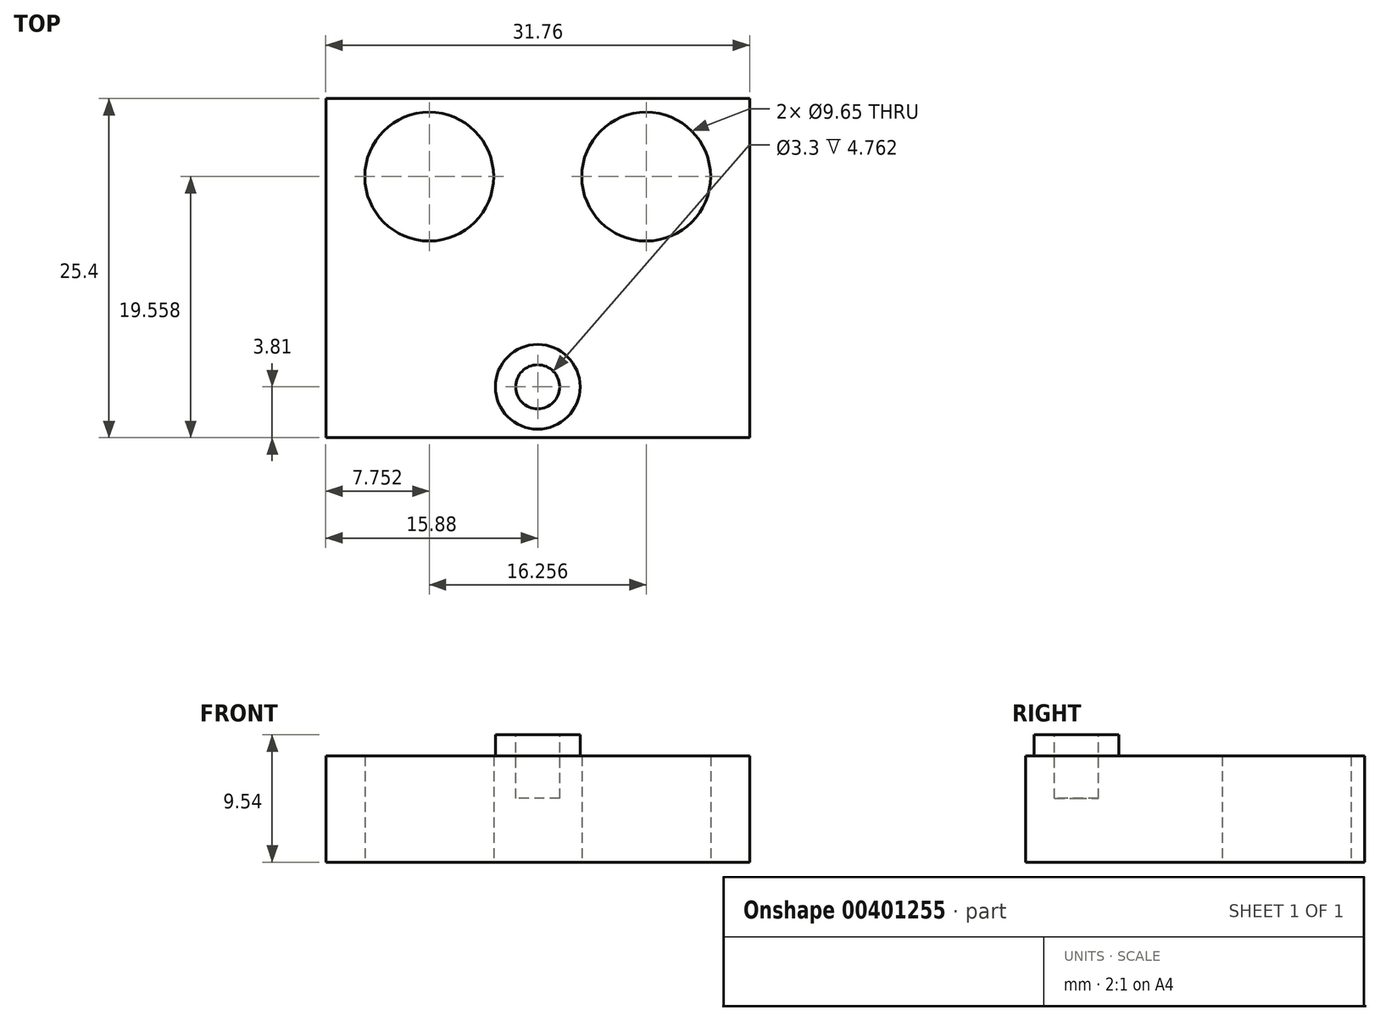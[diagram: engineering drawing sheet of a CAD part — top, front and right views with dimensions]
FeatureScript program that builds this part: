
annotation { "Feature Type Name" : "Feature", "Feature Type Description" : "" }
export const myFeature = defineFeature(function(context is Context, id is Id, definition is map)
    precondition{}
    {
        {
            var Q0;
            Q0=qCreatedBy(makeId("Top.planeOp"),FACE);
            var sketch = newSketch(context, id + "F0", { "sketchPlane" : qUnion([Q0])});
            skLineSegment(sketch, "E0.bottom", {"start": v(-15.88, 12.7) * mm, "end": v(15.88, 12.7) * mm});
            skLineSegment(sketch, "E0.top", {"start": v(-15.88, -12.7) * mm, "end": v(15.88, -12.7) * mm});
            skLineSegment(sketch, "E0.left", {"start": v(-15.88, 12.7) * mm, "end": v(-15.88, -12.7) * mm});
            skLineSegment(sketch, "E0.right", {"start": v(15.88, 12.7) * mm, "end": v(15.88, -12.7) * mm});
            skPoint(sketch, "E0.middle", {"position": v(0, 0) * mm});
            skCircle(sketch, "E1", {"center": v(-8.13, 6.86) * mm, "radius": 4.83 * mm});
            skCircle(sketch, "E2", {"center": v(8.13, 6.86) * mm, "radius": 4.83 * mm});
            skSolve(sketch);
        }
        {
            var Q0;
            Q0 = qSketchRegion(id + "F0", true);
            extrude(context, id + "F1", {"entities" : qUnion([Q0]), "depth" : 7.95 * mm});
        }
        {
            var Q0;
            Q0=makeQuery(id+"F1.opExtrude","CAP_FACE",FACE,{"disambiguationData":[OSD([sQuery(id+"F0.wireOp",EDGE,"E0.bottom"),sQuery(id+"F0.wireOp",EDGE,"E0.top"),sQuery(id+"F0.wireOp",EDGE,"E0.left"),sQuery(id+"F0.wireOp",EDGE,"E0.right"),sQuery(id+"F0.wireOp",EDGE,"E1"),sQuery(id+"F0.wireOp",EDGE,"E2")])],"isStart":false});
            var sketch = newSketch(context, id + "F2", { "sketchPlane" : qUnion([Q0])});
            skCircle(sketch, "E3", {"center": v(0, -8.9) * mm, "radius": 3.18 * mm});
            skSolve(sketch);
        }
        {
            var Q0;
            Q0 = qSketchRegion(id + "F2", true);
            extrude(context, id + "F3", {"entities" : qUnion([Q0]), "operationType" : NewBodyOperationType.ADD, "depth" : 1.59 * mm});
        }
        {
            var Q0;
            Q0=makeQuery(id+"F3.opExtrude","CAP_FACE",FACE,{"disambiguationData":[OSD([sQuery(id+"F2.wireOp",EDGE,"E3")])],"isStart":false});
            var sketch = newSketch(context, id + "F4", { "sketchPlane" : qUnion([Q0])});
            skCircle(sketch, "E4", {"center": v(0, -8.9) * mm, "radius": 1.65 * mm});
            skSolve(sketch);
        }
        {
            var Q0;
            Q0 = qSketchRegion(id + "F4", true);
            extrude(context, id + "F5", {"entities" : qUnion([Q0]), "operationType" : NewBodyOperationType.REMOVE, "oppositeDirection" : true, "depth" : 4.76 * mm});
        }
    });
